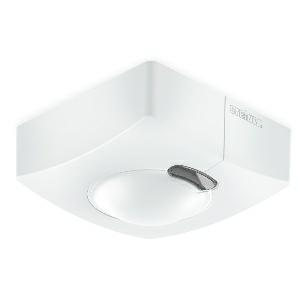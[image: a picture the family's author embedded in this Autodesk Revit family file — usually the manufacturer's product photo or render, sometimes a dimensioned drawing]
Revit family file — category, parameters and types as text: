
# Revit family: hf_3360_057312
name_source: partatom
category: Elektroinstallationen
revit_build: Autodesk Revit 2016 (Build: 20190508_0715(x64)
units: mm (PartAtom-declared; Revit-internal decimal feet)

## family parameters
Basisbauteil = Fläche
Beim Laden mit Abzugskörper schneiden = Nein
Bemaßung runder Anschluss = Durchmesser verwenden
Beschriftungsausrichtung beibehalten = Nein
Gemeinsam genutzt = Nein
Raumberechnungspunkt = Nein
Teiletyp = Normal

## types (1)
- HF 3360
    Apparent Load = 0 VA
    Beschreibung = Type: Motion detectors; Dimensions (L x W x H): 52 x 95 x 95 mm; Mains power supply: 12 – 22,5 V; Power consumption: 0,5 W; Sensor Technology: High frequency; Application, place: Indoors; Application, room: function room / ancillary room, stairwell, WC / washroom, multi-storey / underground car park, Indoors; Installation site: wall, ceiling, corner; Installation: Surface wiring; HF-system: 5,8 GHz; Electronic scalability: Yes; Mechanical scalability: No; Mounting height: 2,00 – 4,00 m; Optimum mounting height: 2,8 m; Detection: also through glass, wood and stud walls; Detection angle: 360 °; Angle of aperture: 160 °; Sneak-by guard: Yes; Reach, radial: Ø 8 m (50 m²); Reach, tangential: Ø 8 m (50 m²); Twilight setting TEACH: No; Twilight setting: 2 – 1000 lx; Control output, Dali: Addressable/slave; Constant-lighting control: No; Basic light level function: No; With bus coupling: Yes; Settings via: Bus; With remote control: No; IP-rating: IP54; Material: Plastic; Ambient temperature: -20 – 50 °C; Colour: white; Colour, RAL: 9003; Manufacturer's Warranty: 5 years; Version: DALI-2 IPD - surface, sq.; PU1, EAN: 4007841057312
    Height = 95 mm
    Hersteller = Steinel
    Length = 52 mm  [stored 0.170604 ft]
    ModVariant = Nein
    Modell = 057312
    Mounting Type = Surface mounted
    Number of Poles = 1
    OnlyDefault = Ja
    Power Factor = 1
    Product Name = HF 3360
    Product group = Sensor-switched indoor light
    ProductGroupID = 30
    Protection Class = Protection class
    Protection Degree = IP 54
    RlxData = <blob elided: 25581 chars, md5=73e095d6>
    SensorDataFile = {"IESDataFiles":[]}
    Typenbild = produkt1_057312.jpg
    Typenkommentare = Product without accessories
    URL = http://relux.com
    VarID = ---
    Voltage = 0 V
    Vorgabe-Ansicht = 1800 mm
    Weight = 0.00 kg
    Width = 95 mm

note: [stored X ft] marks values corroborated as IEEE doubles in the binary element streams (Revit-internal decimal feet)

## geometry (parser evidence)
native form markers: Blend x4, Sweep x13
no freeform markers — native parametric forms only
